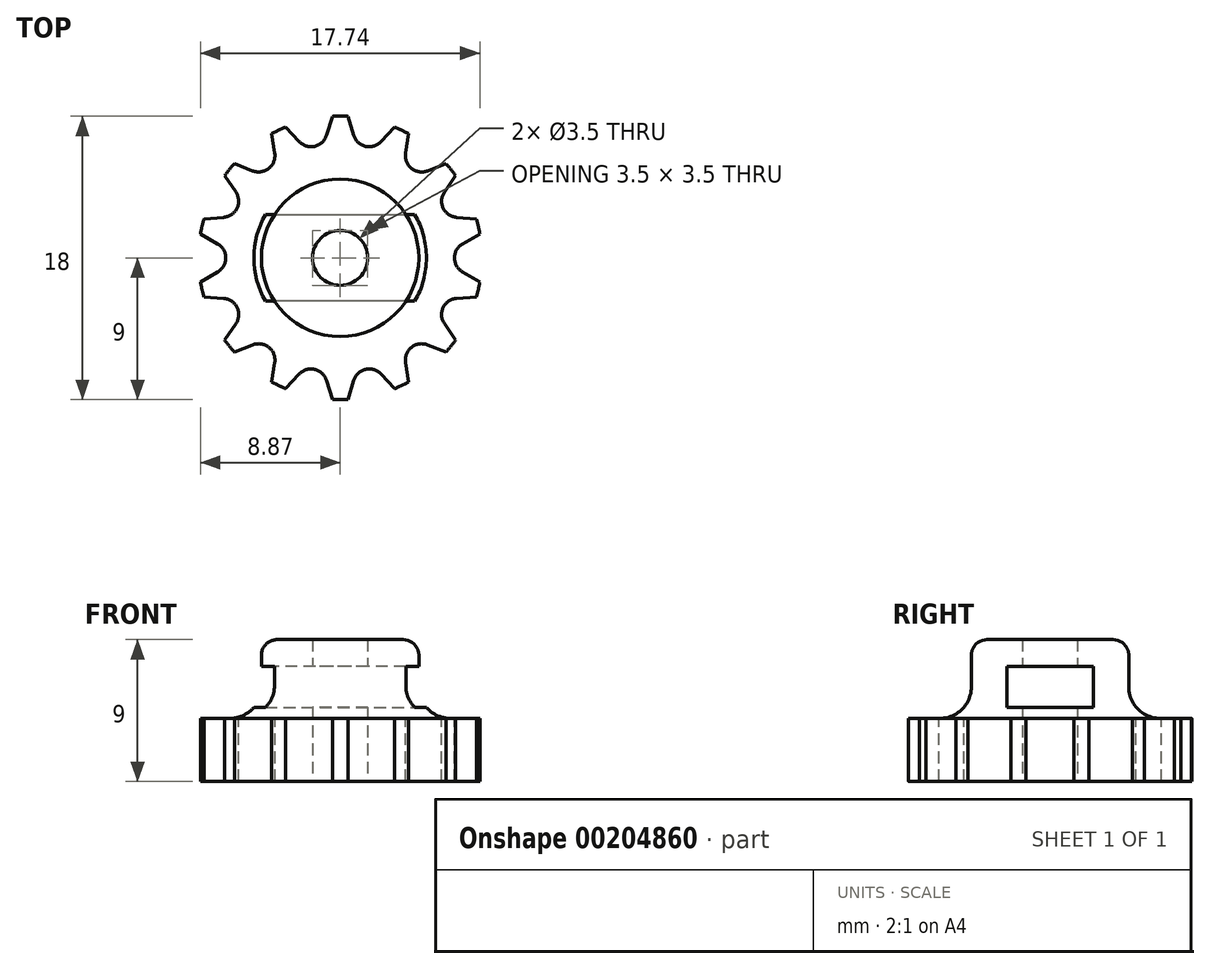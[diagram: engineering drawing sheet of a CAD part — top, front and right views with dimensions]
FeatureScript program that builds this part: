
annotation { "Feature Type Name" : "Feature", "Feature Type Description" : "" }
export const myFeature = defineFeature(function(context is Context, id is Id, definition is map)
    precondition{}
    {
        {
            var Q0;
            Q0=qCreatedBy(makeId("Front.planeOp"),FACE);
            var sketch = newSketch(context, id + "F0", { "sketchPlane" : qUnion([Q0])});
            skLineSegment(sketch, "E0", {"start": v(0, -6) * mm, "end": v(-9, -6) * mm});
            skLineSegment(sketch, "E1", {"start": v(0, -6) * mm, "end": v(0, 3) * mm});
            skLineSegment(sketch, "E2", {"start": v(0, 3) * mm, "end": v(-5, 3) * mm});
            skLineSegment(sketch, "E3", {"start": v(-5, 3) * mm, "end": v(-5, -2) * mm});
            skLineSegment(sketch, "E4", {"start": v(-9, -2) * mm, "end": v(-5, -2) * mm});
            skLineSegment(sketch, "E5", {"start": v(-9, -2) * mm, "end": v(-9, -6) * mm});
            skSolve(sketch);
        }
        {
            var Q0;
            Q0=makeQuery(id+"F0.imprint","IMPRINT",FACE,{"disambiguationData":[TD([[makeQuery(id+"F0.imprint","IMPRINT",EDGE,{"derivedFrom":sQuery(id+"F0.wireOp",EDGE,"E0")}),-1.0]])]});
            var Q1;
            Q1=sQuery(id+"F0.wireOp",EDGE,"E1");
            revolve(context, id + "F1", {"entities" : qUnion([Q0]), "axis" : qUnion([Q1]), "revolveType" : RevolveType.FULL});
        }
        {
            var Q0;
            Q0=qCreatedBy(makeId("Top.planeOp"),FACE);
            var sketch = newSketch(context, id + "F2", { "sketchPlane" : qUnion([Q0])});
            skLineSegment(sketch, "E6", {"start": v(-10.87, 2.75) * mm, "end": v(14.6, 2.75) * mm});
            skLineSegment(sketch, "E7", {"start": v(14.6, 2.75) * mm, "end": v(14.6, -2.75) * mm});
            skLineSegment(sketch, "E8", {"start": v(14.6, -2.75) * mm, "end": v(-10.87, -2.75) * mm});
            skLineSegment(sketch, "E9", {"start": v(-10.87, 2.75) * mm, "end": v(-10.87, -2.75) * mm});
            skSolve(sketch);
        }
        {
            var Q0;
            Q0=qCreatedBy(makeId("Top.planeOp"),FACE);
            var sketch = newSketch(context, id + "F3", { "sketchPlane" : qUnion([Q0])});
            skCircle(sketch, "E10", {"center": v(0, 0) * mm, "radius": 1.75 * mm});
            skSolve(sketch);
        }
        {
            var Q0;
            Q0=makeQuery(id+"F3.imprint","IMPRINT",FACE,{"disambiguationData":[TD([[makeQuery(id+"F3.imprint","IMPRINT",EDGE,{"derivedFrom":sQuery(id+"F3.wireOp",EDGE,"E10")}),1.0]])]});
            extrude(context, id + "F4", {"entities" : qUnion([Q0]), "endBound" : BoundingType.SYMMETRIC, "depth" : 25 * mm});
        }
        {
            var Q0;
            Q0=makeQuery(id+"F4.opExtrude","SWEPT_BODY",BODY,{"disambiguationData":[OSD([sQuery(id+"F3.wireOp",EDGE,"E10")])]});
            var Q1;
            Q1=makeQuery(id+"F1.opRevolve","SWEPT_BODY",BODY,{"disambiguationData":[OSD([sQuery(id+"F0.wireOp",EDGE,"E0"),sQuery(id+"F0.wireOp",EDGE,"hmLDlmhl-fUHp-Yytk-PDIj-Sccdh0N3rT8E"),sQuery(id+"F0.wireOp",EDGE,"E1"),sQuery(id+"F0.wireOp",EDGE,"E2"),sQuery(id+"F0.wireOp",EDGE,"E3"),sQuery(id+"F0.wireOp",EDGE,"E4")])]});
            booleanBodies(context, id + "F5", {"operationType" : BooleanOperationType.SUBTRACTION, "tools" : qUnion([Q0]), "targets" : qUnion([Q1])});
        }
        {
            var Q0;
            Q0=makeQuery(id+"F1.opRevolve","SWEPT_EDGE",EDGE,{"disambiguationData":[OSD([sQuery(id+"F0.wireOp",EDGE,"E3"),sQuery(id+"F0.wireOp",EDGE,"E4")])]});
            fillet(context, id + "F6", {"entities" : qUnion([Q0]), "radius" : 2 * mm, "tangentPropagation" : true, "allowEdgeOverflow" : false});
        }
        {
            var Q0;
            Q0=qCreatedBy(makeId("Top.planeOp"),FACE);
            var sketch = newSketch(context, id + "F7", { "sketchPlane" : qUnion([Q0])});
            skLineSegment(sketch, "E11", {"start": v(-7.78, 0.9) * mm, "end": v(-10.5, 2.46) * mm});
            skLineSegment(sketch, "E12", {"start": v(-10.5, 2.46) * mm, "end": v(-10.5, -2.46) * mm});
            skLineSegment(sketch, "E13", {"start": v(-10.5, -2.46) * mm, "end": v(-7.78, -0.9) * mm});
            skLineSegment(sketch, "E14.1.0", {"start": v(-7.4, -2.57) * mm, "end": v(-10.53, -2.34) * mm});
            skLineSegment(sketch, "E14.1.1", {"start": v(-10.53, -2.34) * mm, "end": v(-8.4, -6.77) * mm});
            skLineSegment(sketch, "E14.1.2", {"start": v(-8.4, -6.77) * mm, "end": v(-6.62, -4.18) * mm});
            skLineSegment(sketch, "E14.2.0", {"start": v(-5.55, -5.53) * mm, "end": v(-8.47, -6.67) * mm});
            skLineSegment(sketch, "E14.2.1", {"start": v(-8.47, -6.67) * mm, "end": v(-4.62, -9.74) * mm});
            skLineSegment(sketch, "E14.2.2", {"start": v(-4.62, -9.74) * mm, "end": v(-4.15, -6.64) * mm});
            skLineSegment(sketch, "E14.3.0", {"start": v(-2.6, -7.39) * mm, "end": v(-4.74, -9.69) * mm});
            skLineSegment(sketch, "E14.3.1", {"start": v(-4.74, -9.69) * mm, "end": v(0.06, -10.78) * mm});
            skLineSegment(sketch, "E14.3.2", {"start": v(0.06, -10.78) * mm, "end": v(-0.86, -7.79) * mm});
            skLineSegment(sketch, "E14.4.0", {"start": v(0.86, -7.79) * mm, "end": v(-0.06, -10.78) * mm});
            skLineSegment(sketch, "E14.4.1", {"start": v(-0.06, -10.78) * mm, "end": v(4.74, -9.69) * mm});
            skLineSegment(sketch, "E14.4.2", {"start": v(4.74, -9.69) * mm, "end": v(2.6, -7.39) * mm});
            skLineSegment(sketch, "E14.5.0", {"start": v(4.15, -6.64) * mm, "end": v(4.62, -9.74) * mm});
            skLineSegment(sketch, "E14.5.1", {"start": v(4.62, -9.74) * mm, "end": v(8.47, -6.67) * mm});
            skLineSegment(sketch, "E14.5.2", {"start": v(8.47, -6.67) * mm, "end": v(5.55, -5.53) * mm});
            skLineSegment(sketch, "E14.6.0", {"start": v(6.62, -4.18) * mm, "end": v(8.4, -6.77) * mm});
            skLineSegment(sketch, "E14.6.1", {"start": v(8.4, -6.77) * mm, "end": v(10.53, -2.34) * mm});
            skLineSegment(sketch, "E14.6.2", {"start": v(10.53, -2.34) * mm, "end": v(7.4, -2.57) * mm});
            skLineSegment(sketch, "E14.7.0", {"start": v(7.78, -0.9) * mm, "end": v(10.5, -2.46) * mm});
            skLineSegment(sketch, "E14.7.1", {"start": v(10.5, -2.46) * mm, "end": v(10.5, 2.46) * mm});
            skLineSegment(sketch, "E14.7.2", {"start": v(10.5, 2.46) * mm, "end": v(7.78, 0.9) * mm});
            skLineSegment(sketch, "E14.8.0", {"start": v(7.4, 2.57) * mm, "end": v(10.53, 2.34) * mm});
            skLineSegment(sketch, "E14.8.1", {"start": v(10.53, 2.34) * mm, "end": v(8.4, 6.77) * mm});
            skLineSegment(sketch, "E14.8.2", {"start": v(8.4, 6.77) * mm, "end": v(6.62, 4.18) * mm});
            skLineSegment(sketch, "E14.9.0", {"start": v(5.55, 5.53) * mm, "end": v(8.47, 6.67) * mm});
            skLineSegment(sketch, "E14.9.1", {"start": v(8.47, 6.67) * mm, "end": v(4.62, 9.74) * mm});
            skLineSegment(sketch, "E14.9.2", {"start": v(4.62, 9.74) * mm, "end": v(4.15, 6.64) * mm});
            skLineSegment(sketch, "E14.10.0", {"start": v(2.6, 7.39) * mm, "end": v(4.74, 9.69) * mm});
            skLineSegment(sketch, "E14.10.1", {"start": v(4.74, 9.69) * mm, "end": v(-0.06, 10.78) * mm});
            skLineSegment(sketch, "E14.10.2", {"start": v(-0.06, 10.78) * mm, "end": v(0.86, 7.79) * mm});
            skLineSegment(sketch, "E14.11.0", {"start": v(-0.86, 7.79) * mm, "end": v(0.06, 10.78) * mm});
            skLineSegment(sketch, "E14.11.1", {"start": v(0.06, 10.78) * mm, "end": v(-4.74, 9.69) * mm});
            skLineSegment(sketch, "E14.11.2", {"start": v(-4.74, 9.69) * mm, "end": v(-2.6, 7.39) * mm});
            skLineSegment(sketch, "E14.12.0", {"start": v(-4.15, 6.64) * mm, "end": v(-4.62, 9.74) * mm});
            skLineSegment(sketch, "E14.12.1", {"start": v(-4.62, 9.74) * mm, "end": v(-8.47, 6.67) * mm});
            skLineSegment(sketch, "E14.12.2", {"start": v(-8.47, 6.67) * mm, "end": v(-5.55, 5.53) * mm});
            skLineSegment(sketch, "E14.13.0", {"start": v(-6.62, 4.18) * mm, "end": v(-8.4, 6.77) * mm});
            skLineSegment(sketch, "E14.13.1", {"start": v(-8.4, 6.77) * mm, "end": v(-10.53, 2.34) * mm});
            skLineSegment(sketch, "E14.13.2", {"start": v(-10.53, 2.34) * mm, "end": v(-7.4, 2.57) * mm});
            skPoint(sketch, "E14.center", {"position": v(0, 0) * mm});
            skPoint(sketch, "E15.visualSharp", {"position": v(-1.39, 6.08) * mm});
            skArc(sketch, "E15.filletArc", {"start": v(-2.6, 7.39) * mm, "mid": v(-1.62, 7.08) * mm, "end": v(-0.86, 7.79) * mm});
            skPoint(sketch, "E16.visualSharp", {"position": v(1.39, 6.08) * mm});
            skArc(sketch, "E16.filletArc", {"start": v(0.86, 7.79) * mm, "mid": v(1.62, 7.08) * mm, "end": v(2.6, 7.39) * mm});
            skPoint(sketch, "E17.visualSharp", {"position": v(3.89, 4.88) * mm});
            skArc(sketch, "E17.filletArc", {"start": v(4.15, 6.64) * mm, "mid": v(4.53, 5.68) * mm, "end": v(5.55, 5.53) * mm});
            skPoint(sketch, "E18.visualSharp", {"position": v(5.62, 2.7) * mm});
            skArc(sketch, "E18.filletArc", {"start": v(6.62, 4.18) * mm, "mid": v(6.55, 3.15) * mm, "end": v(7.4, 2.57) * mm});
            skPoint(sketch, "E19.visualSharp", {"position": v(6.24, 0) * mm});
            skArc(sketch, "E19.filletArc", {"start": v(7.78, 0.9) * mm, "mid": v(7.27, 0) * mm, "end": v(7.78, -0.9) * mm});
            skPoint(sketch, "E20.visualSharp", {"position": v(5.62, -2.7) * mm});
            skArc(sketch, "E20.filletArc", {"start": v(7.4, -2.57) * mm, "mid": v(6.55, -3.15) * mm, "end": v(6.62, -4.18) * mm});
            skPoint(sketch, "E21.visualSharp", {"position": v(3.89, -4.88) * mm});
            skArc(sketch, "E21.filletArc", {"start": v(5.55, -5.53) * mm, "mid": v(4.53, -5.68) * mm, "end": v(4.15, -6.64) * mm});
            skPoint(sketch, "E22.visualSharp", {"position": v(1.39, -6.08) * mm});
            skArc(sketch, "E22.filletArc", {"start": v(2.6, -7.39) * mm, "mid": v(1.62, -7.08) * mm, "end": v(0.86, -7.79) * mm});
            skPoint(sketch, "E23.visualSharp", {"position": v(-1.39, -6.08) * mm});
            skArc(sketch, "E23.filletArc", {"start": v(-0.86, -7.79) * mm, "mid": v(-1.62, -7.08) * mm, "end": v(-2.6, -7.39) * mm});
            skPoint(sketch, "E24.visualSharp", {"position": v(-3.89, -4.88) * mm});
            skArc(sketch, "E24.filletArc", {"start": v(-4.15, -6.64) * mm, "mid": v(-4.53, -5.68) * mm, "end": v(-5.55, -5.53) * mm});
            skPoint(sketch, "E25.visualSharp", {"position": v(-5.62, -2.7) * mm});
            skArc(sketch, "E25.filletArc", {"start": v(-6.62, -4.18) * mm, "mid": v(-6.55, -3.15) * mm, "end": v(-7.4, -2.57) * mm});
            skPoint(sketch, "E26.visualSharp", {"position": v(-6.24, 0) * mm});
            skArc(sketch, "E26.filletArc", {"start": v(-7.78, -0.9) * mm, "mid": v(-7.27, 0) * mm, "end": v(-7.78, 0.9) * mm});
            skPoint(sketch, "E27.visualSharp", {"position": v(-5.62, 2.7) * mm});
            skArc(sketch, "E27.filletArc", {"start": v(-7.4, 2.57) * mm, "mid": v(-6.55, 3.15) * mm, "end": v(-6.62, 4.18) * mm});
            skPoint(sketch, "E28.visualSharp", {"position": v(-3.89, 4.88) * mm});
            skArc(sketch, "E28.filletArc", {"start": v(-5.55, 5.53) * mm, "mid": v(-4.53, 5.68) * mm, "end": v(-4.15, 6.64) * mm});
            skSolve(sketch);
        }
        {
            var Q0;
            Q0=qSketchRegion(id+"F7",true);
            extrude(context, id + "F8", {"entities" : qUnion([Q0]), "operationType" : NewBodyOperationType.REMOVE, "oppositeDirection" : true, "depth" : 10 * mm});
        }
        {
            var Q0;
            Q0=makeQuery(id+"F2.imprint","IMPRINT",FACE,{"disambiguationData":[TD([[makeQuery(id+"F2.imprint","IMPRINT",EDGE,{"derivedFrom":sQuery(id+"F2.wireOp",EDGE,"E6")}),-1.0]])]});
            extrude(context, id + "F9", {"entities" : qUnion([Q0]), "operationType" : NewBodyOperationType.REMOVE, "endBound" : BoundingType.SYMMETRIC, "depth" : 2.6 * mm});
        }
        {
            var Q0;
            Q0=makeQuery(id+"F1.opRevolve","SWEPT_EDGE",EDGE,{"disambiguationData":[OSD([sQuery(id+"F0.wireOp",EDGE,"E2"),sQuery(id+"F0.wireOp",EDGE,"E3")])]});
            fillet(context, id + "F10", {"entities" : qUnion([Q0]), "radius" : 1 * mm, "tangentPropagation" : true, "allowEdgeOverflow" : false});
        }
    });
